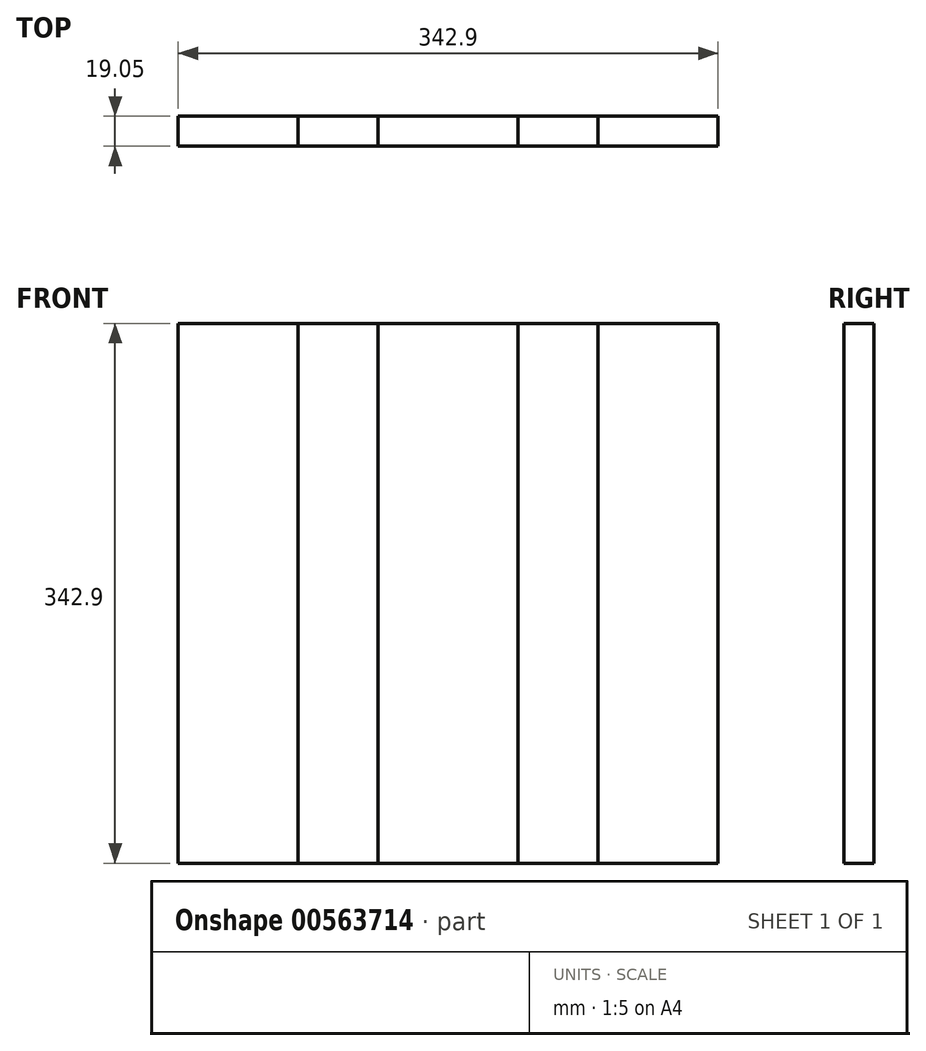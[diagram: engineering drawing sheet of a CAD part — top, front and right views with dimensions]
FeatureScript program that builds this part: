
annotation { "Feature Type Name" : "Feature", "Feature Type Description" : "" }
export const myFeature = defineFeature(function(context is Context, id is Id, definition is map)
    precondition{}
    {
        {
            var Q0;
            Q0=qCreatedBy(makeId("Front.planeOp"),FACE);
            var sketch = newSketch(context, id + "F0", { "sketchPlane" : qUnion([Q0])});
            skLineSegment(sketch, "E0.bottom", {"start": v(171.45, -171.45) * mm, "end": v(-171.45, -171.45) * mm});
            skLineSegment(sketch, "E0.top", {"start": v(171.45, 171.45) * mm, "end": v(-171.45, 171.45) * mm});
            skLineSegment(sketch, "E0.left", {"start": v(171.45, -171.45) * mm, "end": v(171.45, 171.45) * mm});
            skLineSegment(sketch, "E0.right", {"start": v(-171.45, -171.45) * mm, "end": v(-171.45, 171.45) * mm});
            skPoint(sketch, "E0.middle", {"position": v(0, 0) * mm});
            skSolve(sketch);
        }
        {
            var Q0;
            Q0=qCreatedBy(makeId("Front.planeOp"),FACE);
            var sketch = newSketch(context, id + "F1", { "sketchPlane" : qUnion([Q0])});
            skLineSegment(sketch, "E1.0.0", {"start": v(171.45, -171.45) * mm, "end": v(171.45, 171.45) * mm});
            skLineSegment(sketch, "E1.0.1", {"start": v(171.45, 171.45) * mm, "end": v(-171.45, 171.45) * mm});
            skLineSegment(sketch, "E1.0.2", {"start": v(-171.45, 171.45) * mm, "end": v(-171.45, -171.45) * mm});
            skLineSegment(sketch, "E1.0.3", {"start": v(-171.45, -171.45) * mm, "end": v(171.45, -171.45) * mm});
            skLineSegment(sketch, "E2", {"start": v(-95.25, 171.45) * mm, "end": v(-95.25, -171.45) * mm});
            skLineSegment(sketch, "E3", {"start": v(-44.45, 171.45) * mm, "end": v(-44.45, -171.45) * mm});
            skLineSegment(sketch, "E4", {"start": v(95.25, 171.45) * mm, "end": v(95.25, -171.45) * mm});
            skLineSegment(sketch, "E5", {"start": v(44.45, 171.45) * mm, "end": v(44.45, -171.45) * mm});
            skSolve(sketch);
        }
        {
            var Q0;
            {var subQ0=sQuery(id+"F1.wireOp",EDGE,"E1.0.0");Q0=makeQuery(id+"F1.imprint","IMPRINT",FACE,{"disambiguationData":[TD([[makeQuery(id+"F1.imprint","IMPRINT",EDGE,{"derivedFrom":subQ0}),1.0]])]});}
            var Q1;
            {var subQ0=sQuery(id+"F1.wireOp",EDGE,"E1.0.2");Q1=makeQuery(id+"F1.imprint","IMPRINT",FACE,{"disambiguationData":[TD([[makeQuery(id+"F1.imprint","IMPRINT",EDGE,{"derivedFrom":subQ0}),1.0]])]});}
            extrude(context, id + "F2", {"entities" : qUnion([Q0, Q1]), "depth" : 19.05 * mm, "offsetDistance" : 25.4 * mm});
        }
        {
            var Q0;
            {var subQ0=sQuery(id+"F1.wireOp",EDGE,"E2");Q0=makeQuery(id+"F1.imprint","IMPRINT",FACE,{"disambiguationData":[TD([[makeQuery(id+"F1.imprint","IMPRINT",EDGE,{"derivedFrom":subQ0}),1.0]])]});}
            var Q1;
            {var subQ0=sQuery(id+"F1.wireOp",EDGE,"E4");Q1=makeQuery(id+"F1.imprint","IMPRINT",FACE,{"disambiguationData":[TD([[makeQuery(id+"F1.imprint","IMPRINT",EDGE,{"derivedFrom":subQ0}),-1.0]])]});}
            extrude(context, id + "F3", {"entities" : qUnion([Q0, Q1]), "depth" : 19.05 * mm, "offsetDistance" : 25.4 * mm});
        }
        {
            var Q0;
            {var subQ0=sQuery(id+"F1.wireOp",EDGE,"E3");Q0=makeQuery(id+"F1.imprint","IMPRINT",FACE,{"disambiguationData":[TD([[makeQuery(id+"F1.imprint","IMPRINT",EDGE,{"derivedFrom":subQ0}),1.0]])]});}
            extrude(context, id + "F4", {"entities" : qUnion([Q0]), "depth" : 19.05 * mm, "offsetDistance" : 25.4 * mm});
        }
    });
